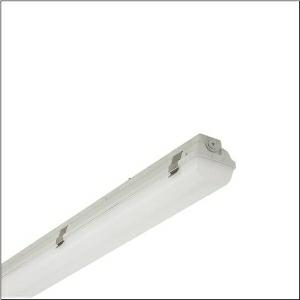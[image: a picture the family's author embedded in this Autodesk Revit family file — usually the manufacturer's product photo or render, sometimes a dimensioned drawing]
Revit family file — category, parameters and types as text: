
# Revit family: monsun_r__21_eco_51fj20mp47a_a802
name_source: partatom
category: Lighting Fixtures
units: mm (PartAtom-declared; Revit-internal decimal feet)

## family parameters
Cut with Voids When Loaded = No
Host = Face
Light Source = No
Part Type = Normal
Room Calculation Point = No
Round Connector Dimension = Use Diameter
Shared = No

## types (1)
- --- (1 x LED, 6600 lm, 50 W, 4000K)
    Apparent Load = 50 VA
    CIE Flux Codes = 40 69 88 88 100
    Color Rendering = 80
    Color Temperature = 4000K
    Default Elevation = 1800 mm
    Description = Monsun® 21 Eco, damp-proof luminaire, primary optical cover: diffuser, of PC, UV-stabilised, frosted, light emission: direct distribution, primary light characteristic: symmetric, installation type: suspended mounting, surface-mounted, LED, rated luminous flux: 6.600lm, luminous efficacy: 132lm/W, light colour: 840, colour temperature: 4000K, control gear: ON/OFF Multilumen, with terminal, 3-pole, max. 2.5mm², mains connection: 220..240V, AC, 50/60Hz, rated input power: 50W, housing, of glass-fibre reinforced polyester, light grey (RAL 7035), length: 1.577mm, width: 90mm, height: 95mm, clip for enclosure, of spring steel V2A, protection rating (complete): IP66, insulation class (complete): insulation class I (protective earthing), certification: CE, UKCA, protection symbol: D, impact resistance: IK08, permissible operating ambient temperature: -20..+35°C, corresponds to IFS (International Featured Standards) requirements for safety and quality in the food industry, contact your sales advisor before using the luminaires in applications with unclear chemical exposure, large temperature fluctuations or condensation-forming humidity, packaging unit: 1 piece
    Height = 103 mm
    Lamp = 1 x LED
    Lamp Light Flux = 6600 lm
    Lamp Power = 50 W
    Lamp count = 1
    Length = 1577 mm
    Luminous efficacy = 132 lm/W
    Manufacturer = Siteco
    ModVariant = No
    Model = 51FJ20MP47A
    Mounting Place = Ceiling
    Mounting Type = Surface mounted
    Number of Poles = 1
    OnlyDefault = Yes
    Power Factor = 1
    Product Name = Monsun® 21 Eco
    Product group = damp-proof luminaire
    ProductGroupID = 300
    Protection Class = Protection class I
    Protection Degree = IP 66
    RLX_Detail_Level = 1
    RLX_Emergency_Light_Flux = 0 lm
    RLX_Emergency_Type = 0
    RLX_Emergency_Type_DB = No
    RlxData = <blob elided: 34137 chars, md5=53118e3f>
    Socket = socket
    Standby Power = 0 W
    System Light Flux = 6600 lm
    System Power = 50 W
    Type Comments = factory setting: luminous flux: 100 % | (ON | ON) | 350 mA
    Type Image = l_1007218.jpg
    URL = http://relux.com
    VarID = @adj_146178
    Voltage = 0 V
    Weight = 0.00 kg
    Width = 90 mm

## geometry (parser evidence)
native form markers: Blend x4, Sweep x13
no freeform markers — native parametric forms only
